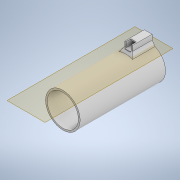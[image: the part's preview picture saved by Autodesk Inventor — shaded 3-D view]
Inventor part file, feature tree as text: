
AUTODESK INVENTOR PART (.ipt)
format: ipt  version: 2021 (Build 250183000, 183)  size: 466,432 bytes
history: native  units: in
note: dims shown in document units (in); Inventor stores cm internally (conversion verified against a paired STEP export)
features: projected_geometry x11, extrude x9, sketch x8, chamfer x4, plane x1, pattern_linear x1
ambient origin geometry x8: Origin, YZ Plane, XZ Plane, XY Plane, X Axis, Y Axis, Z Axis, Center Point
bodies: Solid1 (feature_tree)
feature tree (34):
  extrude  "Extrusion1"  Depth=4.3307in TaperAngle=0.0deg
  plane  "Work Plane1"
  extrude  "Extrusion7"  Depth=4.252in TaperAngle=0.0deg
  extrude  "Extrusion8"  Depth=0.9843in
  extrude  "Extrusion9"  Depth=0.2047in
  extrude  "Extrusion10"  Depth=0.1181in
  extrude  "Extrusion11"  Depth=0.0591in
  extrude  "Extrusion12"  Depth=0.0591in
  pattern_linear  "Rectangular Pattern3"  Spacing1=1.6929in  [1 undecoded]
  extrude  "Extrusion13"  Depth=1.811in
  chamfer  "Chamfer2"  Distance=0.0394in
  chamfer  "Chamfer4"  Distance=0.0098in
  chamfer  "Chamfer5"  Distance=8.2677in
  extrude  "Extrusion14"  Depth=0.248in
  chamfer  "Chamfer6"  Distance=0.3937in
  sketch  "Sketch2"  dims[d2=1.752in d3=4.3307in d4=0.0in]
  sketch  "Sketch9"  dims[d54=1.5748in d55=4.252in d56=0.0in]
  projected_geometry  "Projected Loop7"
  sketch  "Sketch10"  dims[d57=0.3937in d58=0.9843in]
  projected_geometry  "Projected Loop8"
  sketch  "Sketch11"  dims[d59=0.3937in d60=0.0236in d61=0.0in d62=0.0in d63=0.2047in]
  projected_geometry  "Projected Loop9"
  sketch  "Sketch12"  dims[d64=0.126in d65=0.1181in]
  projected_geometry  "Projected Loop10"
  projected_geometry  "Projected Loop11"
  projected_geometry  "Projected Loop12"
  sketch  "Sketch14"  dims[d66=0.0551in d67=0.0in d68=0.0591in]
  projected_geometry  "Projected Loop14"
  projected_geometry  "Projected Loop15"
  sketch  "Sketch16"  dims[d69=0.0591in d70=0.0591in]
  projected_geometry  "Projected Loop16"
  sketch  "Sketch17"  dims[d71=0.9646in d72=0.0in d76=1.6929in d77=0.0in d84=1.811in d85=0.0394in d86=0.0098in d87=0.0in d88=8.2677in d90=0.0787in d92=0.248in d93=0.3937in d94=0.0in d95=0.0787in d96=0.0059in d97=0.0185in d98=0.0787in d99=45.0deg d103=0.1575in d104=0.0787in d105=45.0deg d106=0.0098in d107=0.0787in d108=45.0deg d109=0.5906in d110=0.0315in d111=0.0in d112=0.0315in d113=0.0787in d114=45.0deg d19=0.0197in d20=0.0344in d21=0.0197in d22=0.0344in]
  projected_geometry  "Projected Loop17"
  projected_geometry  "Projected Loop18"
note: 1 required parameter value undecoded (feature->parameter linkage not recoverable at this tier; creation-order binding heuristic only, values carry confidence <= 0.55)
